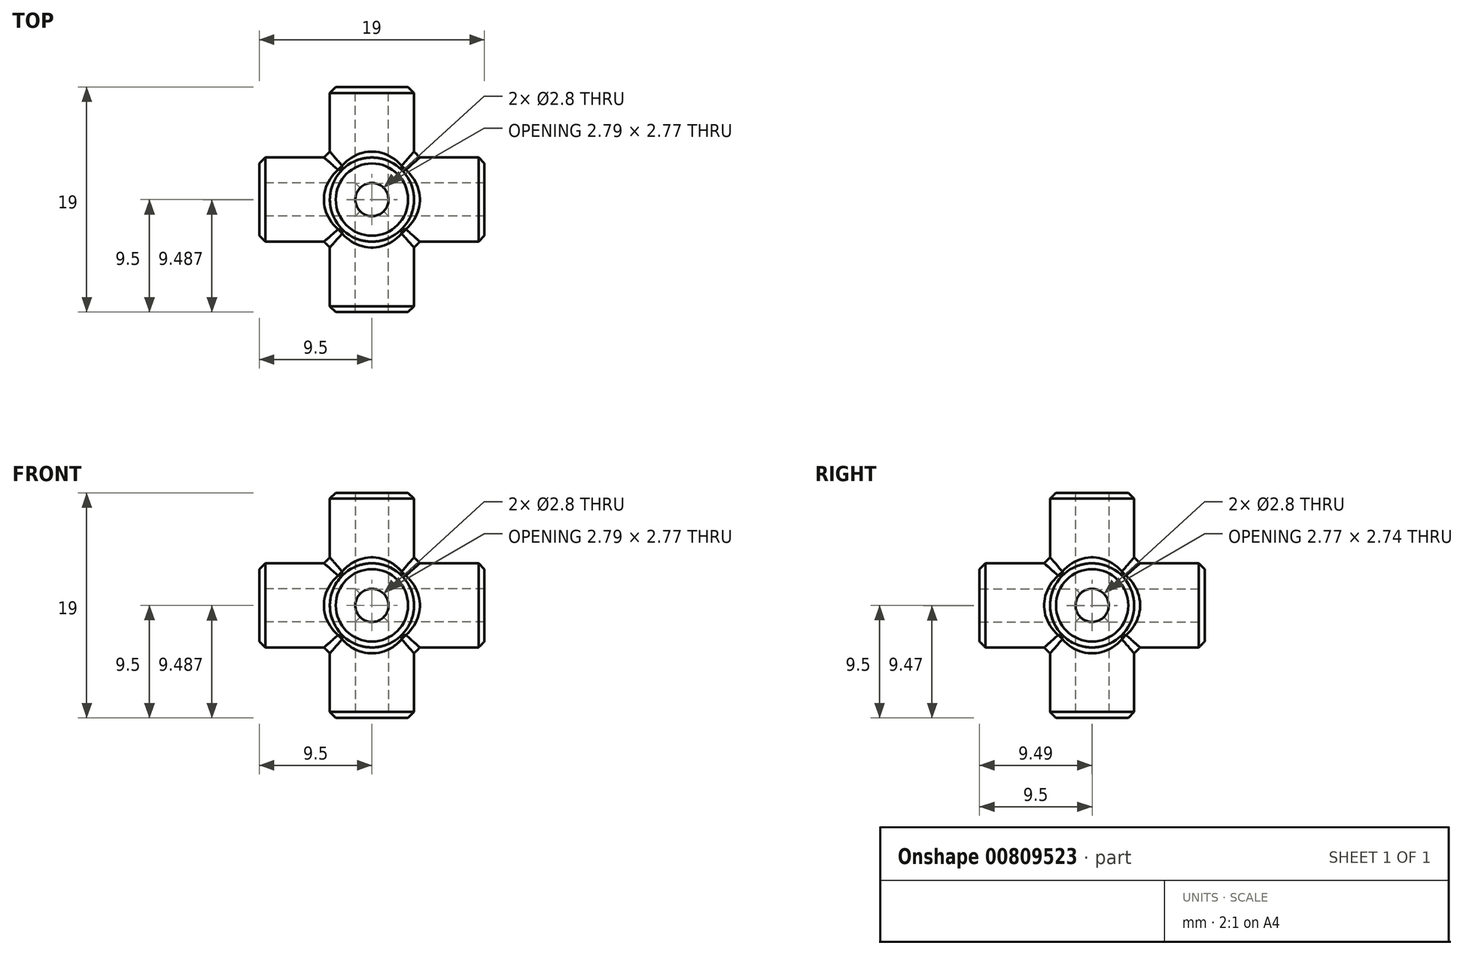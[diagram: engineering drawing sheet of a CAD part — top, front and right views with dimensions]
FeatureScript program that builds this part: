
annotation { "Feature Type Name" : "Feature", "Feature Type Description" : "" }
export const myFeature = defineFeature(function(context is Context, id is Id, definition is map)
    precondition{}
    {
        {
            var Q0;
            Q0=qCreatedBy(makeId("Front.planeOp"),FACE);
            var sketch = newSketch(context, id + "F0", { "sketchPlane" : qUnion([Q0])});
            skCircle(sketch, "E0", {"center": v(0, 0) * mm, "radius": 3.55 * mm});
            skSolve(sketch);
        }
        {
            var Q0;
            Q0=makeQuery(id+"F0.imprint","IMPRINT",FACE,{"disambiguationData":[TD([[makeQuery(id+"F0.imprint","IMPRINT",EDGE,{"derivedFrom":sQuery(id+"F0.wireOp",EDGE,"E0")}),1.0]])]});
            extrude(context, id + "F1", {"entities" : qUnion([Q0]), "endBound" : BoundingType.SYMMETRIC, "depth" : 19 * mm, "offsetDistance" : 25 * mm});
        }
        {
            var Q0;
            Q0=qCreatedBy(makeId("Front.planeOp"),FACE);
            var sketch = newSketch(context, id + "F2", { "sketchPlane" : qUnion([Q0])});
            skCircle(sketch, "E1", {"center": v(0, 0) * mm, "radius": 1.4 * mm});
            skSolve(sketch);
        }
        {
            var Q0;
            Q0=makeQuery(id+"F2.imprint","IMPRINT",FACE,{"disambiguationData":[TD([[makeQuery(id+"F2.imprint","IMPRINT",EDGE,{"derivedFrom":sQuery(id+"F2.wireOp",EDGE,"E1")}),1.0]])]});
            extrude(context, id + "F3", {"entities" : qUnion([Q0]), "endBound" : BoundingType.SYMMETRIC, "depth" : 20 * mm, "offsetDistance" : 25 * mm});
        }
        {
            var Q0;
            Q0=qCreatedBy(makeId("Front.planeOp"),FACE);
            var sketch = newSketch(context, id + "F4", { "sketchPlane" : qUnion([Q0])});
            skLineSegment(sketch, "E2.bottom", {"start": v(0, 0) * mm, "end": v(10, 0) * mm});
            skLineSegment(sketch, "E2.top", {"start": v(0, 10) * mm, "end": v(10, 10) * mm});
            skLineSegment(sketch, "E2.left", {"start": v(0, 0) * mm, "end": v(0, 10) * mm});
            skLineSegment(sketch, "E2.right", {"start": v(10, 0) * mm, "end": v(10, 10) * mm});
            skSolve(sketch);
        }
        {
            var Q0;
            Q0=makeQuery(id+"F4.imprint","IMPRINT",FACE,{"disambiguationData":[TD([[makeQuery(id+"F4.imprint","IMPRINT",EDGE,{"derivedFrom":sQuery(id+"F4.wireOp",EDGE,"E2.bottom")}),1.0]])]});
            extrude(context, id + "F5", {"entities" : qUnion([Q0]), "depth" : 10 * mm, "offsetDistance" : 25 * mm});
        }
        {
            var Q0;
            Q0=qCreatedBy(makeId("Origin.pointOp"),VERTEX);
            var Q1;
            Q1=makeQuery(id+"F5.opExtrude","CAP_VERTEX",VERTEX,{"disambiguationData":[OSD([sQuery(id+"F4.wireOp",EDGE,"E2.top"),sQuery(id+"F4.wireOp",EDGE,"E2.right")])],"isStart":false});
            var Q2;
            Q2=makeQuery(id+"F5.opExtrude","CAP_VERTEX",VERTEX,{"disambiguationData":[OSD([sQuery(id+"F4.wireOp",EDGE,"E2.bottom"),sQuery(id+"F4.wireOp",EDGE,"E2.right")])],"isStart":false});
            cPlane(context, id + "F6", {"entities" : qUnion([Q0, Q1, Q2]), "cplaneType" : CPlaneType.THREE_POINT, "offset" : 25 * mm, "width" : 150 * mm, "height" : 150 * mm});
        }
        {
            var Q0;
            Q0=qCreatedBy(id+"F6.planeOp",FACE);
            var sketch = newSketch(context, id + "F7", { "sketchPlane" : qUnion([Q0])});
            skLineSegment(sketch, "E3", {"start": v(0, 0) * mm, "end": v(14.14, 10) * mm});
            skSolve(sketch);
        }
        {
            var Q0;
            Q0=makeQuery(id+"F5.opExtrude","SWEPT_BODY",BODY,{"disambiguationData":[OSD([sQuery(id+"F4.wireOp",EDGE,"E2.bottom"),sQuery(id+"F4.wireOp",EDGE,"E2.top"),sQuery(id+"F4.wireOp",EDGE,"E2.left"),sQuery(id+"F4.wireOp",EDGE,"E2.right")])]});
            deleteBodies(context, id + "F8", {"entities" : qUnion([Q0])});
        }
        {
            var Q0;
            Q0=makeQuery(id+"F1.opExtrude","SWEPT_BODY",BODY,{"disambiguationData":[OSD([sQuery(id+"F0.wireOp",EDGE,"E0")])]});
            var Q1;
            Q1=makeQuery(id+"F3.opExtrude","SWEPT_BODY",BODY,{"disambiguationData":[OSD([sQuery(id+"F2.wireOp",EDGE,"E1")])]});
            var Q2;
            Q2=sQuery(id+"F7.wireOp",EDGE,"E3");
            circularPattern(context, id + "F9", {"entities" : qUnion([Q0, Q1]), "axis" : qUnion([Q2]), "angle" : 360 * degree, "instanceCount" : 3, "equalSpace" : true});
        }
        {
            var Q0;
            Q0=makeQuery(id+"F9.opPattern","COPY",BODY,{"derivedFrom":makeQuery(id+"F1.opExtrude","SWEPT_BODY",BODY,{"disambiguationData":[OSD([sQuery(id+"F0.wireOp",EDGE,"E0")])]}),"instanceName":"2"});
            var Q1;
            Q1=makeQuery(id+"F9.opPattern","COPY",BODY,{"derivedFrom":makeQuery(id+"F1.opExtrude","SWEPT_BODY",BODY,{"disambiguationData":[OSD([sQuery(id+"F0.wireOp",EDGE,"E0")])]}),"instanceName":"1"});
            var Q2;
            Q2=makeQuery(id+"F1.opExtrude","SWEPT_BODY",BODY,{"disambiguationData":[OSD([sQuery(id+"F0.wireOp",EDGE,"E0")])]});
            booleanBodies(context, id + "F10", {"operationType" : BooleanOperationType.UNION, "tools" : qUnion([Q0, Q1, Q2])});
        }
        {
            var Q0;
            Q0=makeQuery(id+"F9.opPattern","COPY",BODY,{"derivedFrom":makeQuery(id+"F3.opExtrude","SWEPT_BODY",BODY,{"disambiguationData":[OSD([sQuery(id+"F2.wireOp",EDGE,"E1")])]}),"instanceName":"2"});
            var Q1;
            Q1=makeQuery(id+"F3.opExtrude","SWEPT_BODY",BODY,{"disambiguationData":[OSD([sQuery(id+"F2.wireOp",EDGE,"E1")])]});
            var Q2;
            Q2=makeQuery(id+"F9.opPattern","COPY",BODY,{"derivedFrom":makeQuery(id+"F3.opExtrude","SWEPT_BODY",BODY,{"disambiguationData":[OSD([sQuery(id+"F2.wireOp",EDGE,"E1")])]}),"instanceName":"1"});
            var Q3;
            Q3=makeQuery(id+"F9.opPattern","COPY",BODY,{"derivedFrom":makeQuery(id+"F1.opExtrude","SWEPT_BODY",BODY,{"disambiguationData":[OSD([sQuery(id+"F0.wireOp",EDGE,"E0")])]}),"instanceName":"2"});
            booleanBodies(context, id + "F11", {"operationType" : BooleanOperationType.SUBTRACTION, "tools" : qUnion([Q0, Q1, Q2]), "targets" : qUnion([Q3])});
        }
        {
            var Q0;
            {var subQ0=sQuery(id+"F0.wireOp",EDGE,"E0");var subQ1=makeQuery(id+"F1.opExtrude","SWEPT_FACE",FACE,{"disambiguationData":[OSD([subQ0])]});Q0=makeQuery(id+"F10.opBoolean","SPLIT",FACE,{"disambiguationData":[TD([makeQuery(id+"F9.opPattern","COPY",FACE,{"derivedFrom":makeQuery(id+"F1.opExtrude","CAP_FACE",FACE,{"disambiguationData":[OSD([subQ0])],"isStart":false}),"instanceName":"2"})])],"derivedFrom":makeQuery(id+"F9.opPattern","COPY",FACE,{"derivedFrom":subQ1,"instanceName":"2"})});}
            var Q1;
            {var subQ0=sQuery(id+"F0.wireOp",EDGE,"E0");var subQ1=makeQuery(id+"F1.opExtrude","SWEPT_FACE",FACE,{"disambiguationData":[OSD([subQ0])]});Q1=makeQuery(id+"F10.opBoolean","SPLIT",FACE,{"disambiguationData":[TD([makeQuery(id+"F1.opExtrude","CAP_FACE",FACE,{"disambiguationData":[OSD([subQ0])],"isStart":true})])],"derivedFrom":subQ1});}
            var Q2;
            {var subQ0=sQuery(id+"F0.wireOp",EDGE,"E0");var subQ1=makeQuery(id+"F1.opExtrude","SWEPT_FACE",FACE,{"disambiguationData":[OSD([subQ0])]});Q2=makeQuery(id+"F10.opBoolean","SPLIT",FACE,{"disambiguationData":[TD([makeQuery(id+"F9.opPattern","COPY",FACE,{"derivedFrom":makeQuery(id+"F1.opExtrude","CAP_FACE",FACE,{"disambiguationData":[OSD([subQ0])],"isStart":false}),"instanceName":"1"})])],"derivedFrom":makeQuery(id+"F9.opPattern","COPY",FACE,{"derivedFrom":subQ1,"instanceName":"1"})});}
            var Q3;
            {var subQ0=sQuery(id+"F0.wireOp",EDGE,"E0");var subQ1=makeQuery(id+"F1.opExtrude","SWEPT_FACE",FACE,{"disambiguationData":[OSD([subQ0])]});Q3=makeQuery(id+"F10.opBoolean","SPLIT",FACE,{"disambiguationData":[TD([makeQuery(id+"F9.opPattern","COPY",FACE,{"derivedFrom":makeQuery(id+"F1.opExtrude","CAP_FACE",FACE,{"disambiguationData":[OSD([subQ0])],"isStart":true}),"instanceName":"1"})])],"derivedFrom":makeQuery(id+"F9.opPattern","COPY",FACE,{"derivedFrom":subQ1,"instanceName":"1"})});}
            var Q4;
            {var subQ0=sQuery(id+"F0.wireOp",EDGE,"E0");var subQ1=makeQuery(id+"F1.opExtrude","SWEPT_FACE",FACE,{"disambiguationData":[OSD([subQ0])]});Q4=makeQuery(id+"F10.opBoolean","SPLIT",FACE,{"disambiguationData":[TD([makeQuery(id+"F1.opExtrude","CAP_FACE",FACE,{"disambiguationData":[OSD([subQ0])],"isStart":false})])],"derivedFrom":subQ1});}
            var Q5;
            {var subQ0=sQuery(id+"F0.wireOp",EDGE,"E0");var subQ1=makeQuery(id+"F1.opExtrude","SWEPT_FACE",FACE,{"disambiguationData":[OSD([subQ0])]});Q5=makeQuery(id+"F10.opBoolean","SPLIT",FACE,{"disambiguationData":[TD([makeQuery(id+"F9.opPattern","COPY",FACE,{"derivedFrom":makeQuery(id+"F1.opExtrude","CAP_FACE",FACE,{"disambiguationData":[OSD([subQ0])],"isStart":true}),"instanceName":"2"})])],"derivedFrom":makeQuery(id+"F9.opPattern","COPY",FACE,{"derivedFrom":subQ1,"instanceName":"2"})});}
            chamfer(context, id + "F12", {"entities" : qUnion([Q0, Q1, Q2, Q3, Q4, Q5]), "width" : 0.5 * mm, "tangentPropagation" : true});
        }
    });
